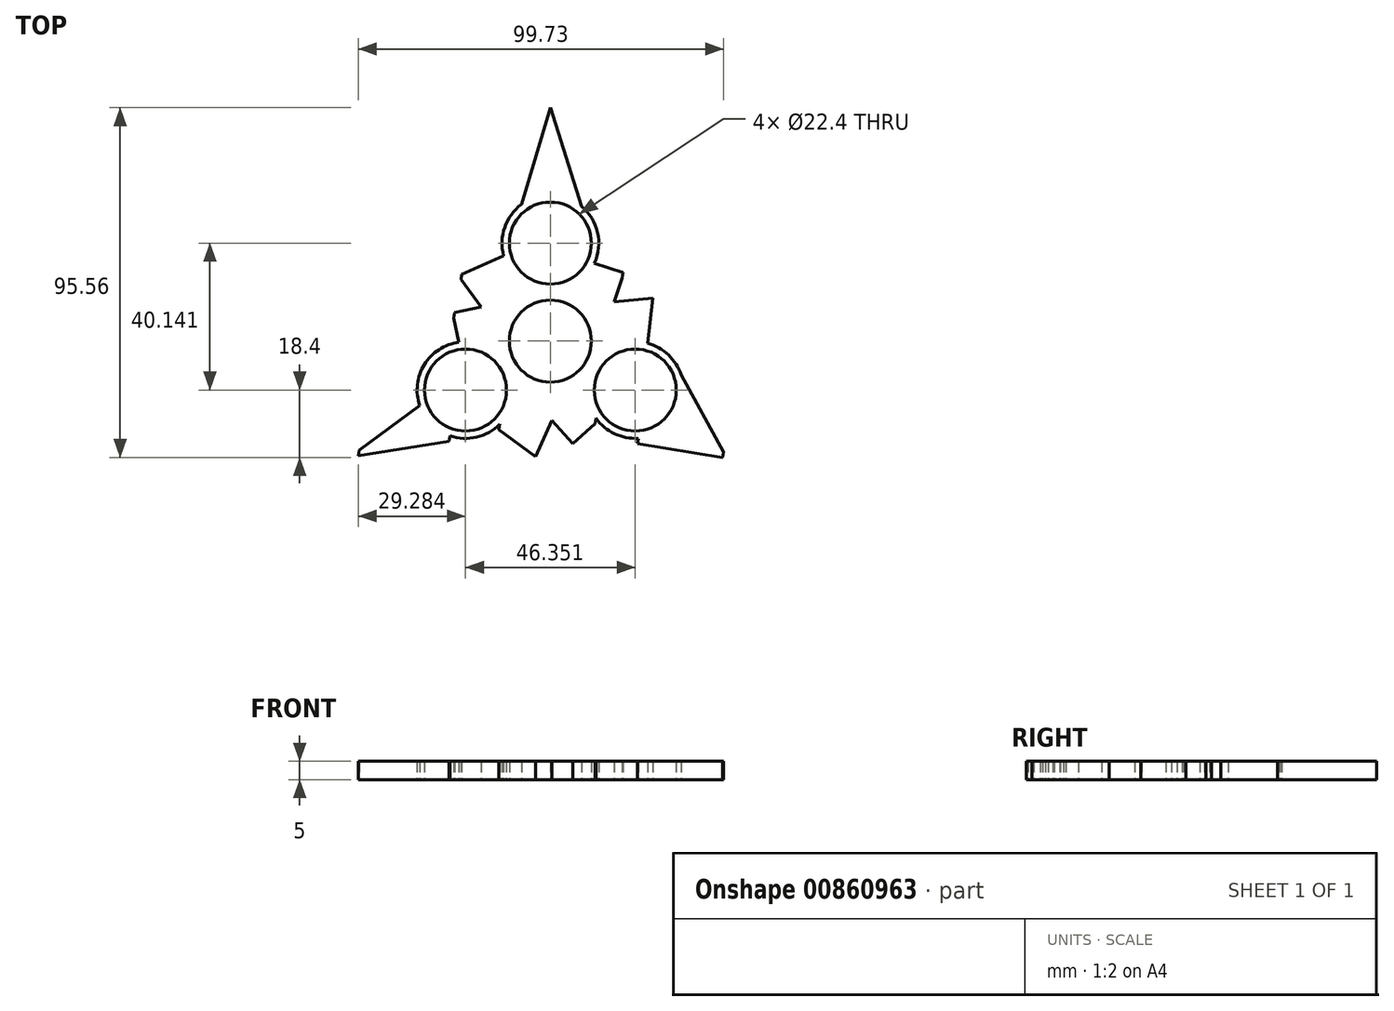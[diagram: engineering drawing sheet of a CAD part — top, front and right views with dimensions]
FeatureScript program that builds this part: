
annotation { "Feature Type Name" : "Feature", "Feature Type Description" : "" }
export const myFeature = defineFeature(function(context is Context, id is Id, definition is map)
    precondition{}
    {
        {
            var Q0;
            Q0=qCreatedBy(makeId("Top.planeOp"),FACE);
            var sketch = newSketch(context, id + "F0", { "sketchPlane" : qUnion([Q0])});
            skCircle(sketch, "E0", {"center": v(0, 0) * mm, "radius": 11.2 * mm});
            skCircle(sketch, "E1", {"center": v(0, 26.76) * mm, "radius": 11.2 * mm});
            skArc(sketch, "E2", {"start": v(12.02, 21.3) * mm, "mid": v(1.06, 39.92) * mm, "end": v(-12.74, 23.3) * mm});
            skArc(sketch, "E3.1.0", {"start": v(-24.46, -0.24) * mm, "mid": v(-35.1, -19.04) * mm, "end": v(-13.81, -22.68) * mm});
            skCircle(sketch, "E3.1.1", {"center": v(-23.18, -13.38) * mm, "radius": 11.2 * mm});
            skArc(sketch, "E3.2.0", {"start": v(12.44, -21.06) * mm, "mid": v(34.04, -20.88) * mm, "end": v(26.55, -0.62) * mm});
            skCircle(sketch, "E3.2.1", {"center": v(23.18, -13.38) * mm, "radius": 11.2 * mm});
            skLineSegment(sketch, "E4", {"start": v(-7.9, 37.34) * mm, "end": v(0, 63.78) * mm});
            skLineSegment(sketch, "E5", {"start": v(0, 63.78) * mm, "end": v(8.56, 36.8) * mm});
            skLineSegment(sketch, "E6", {"start": v(35.72, -9.27) * mm, "end": v(47.27, -30.3) * mm});
            skLineSegment(sketch, "E7", {"start": v(47.27, -30.3) * mm, "end": v(23.98, -26.56) * mm});
            skLineSegment(sketch, "E8", {"start": v(-35.69, -17.6) * mm, "end": v(-52.22, -29.83) * mm});
            skLineSegment(sketch, "E9", {"start": v(-52.22, -29.83) * mm, "end": v(-27.41, -25.88) * mm});
            skLineSegment(sketch, "E10", {"start": v(-12.74, 23.3) * mm, "end": v(-24.17, 18.27) * mm});
            skLineSegment(sketch, "E11", {"start": v(-24.17, 18.27) * mm, "end": v(-17.8, 9.55) * mm});
            skLineSegment(sketch, "E12", {"start": v(-17.8, 9.55) * mm, "end": v(-26.14, 7.8) * mm});
            skLineSegment(sketch, "E13", {"start": v(-26.14, 7.8) * mm, "end": v(-24.46, -0.24) * mm});
            skLineSegment(sketch, "E14.1.0", {"start": v(-13.81, -22.68) * mm, "end": v(-3.74, -30.07) * mm});
            skLineSegment(sketch, "E14.1.1", {"start": v(-3.74, -30.07) * mm, "end": v(0.63, -20.2) * mm});
            skLineSegment(sketch, "E14.1.2", {"start": v(0.63, -20.2) * mm, "end": v(6.31, -26.54) * mm});
            skLineSegment(sketch, "E14.1.3", {"start": v(6.31, -26.54) * mm, "end": v(12.44, -21.06) * mm});
            skLineSegment(sketch, "E14.2.0", {"start": v(26.55, -0.62) * mm, "end": v(27.9, 11.8) * mm});
            skLineSegment(sketch, "E14.2.1", {"start": v(27.9, 11.8) * mm, "end": v(17.17, 10.64) * mm});
            skLineSegment(sketch, "E14.2.2", {"start": v(17.17, 10.64) * mm, "end": v(19.83, 18.74) * mm});
            skLineSegment(sketch, "E14.2.3", {"start": v(19.83, 18.74) * mm, "end": v(12.02, 21.3) * mm});
            skSolve(sketch);
        }
        {
            var Q0;
            Q0=makeQuery(id+"F0.imprint","IMPRINT",FACE,{"disambiguationData":[TD([[makeQuery(id+"F0.imprint","IMPRINT",EDGE,{"derivedFrom":sQuery(id+"F0.wireOp",EDGE,"E0")}),-1.0]])]});
            var Q1;
            {var subQ0=sQuery(id+"F0.wireOp",EDGE,"E8");Q1=makeQuery(id+"F0.imprint","IMPRINT",FACE,{"disambiguationData":[TD([[makeQuery(id+"F0.imprint","IMPRINT",EDGE,{"derivedFrom":subQ0}),1.0]])]});}
            var Q2;
            {var subQ0=sQuery(id+"F0.wireOp",EDGE,"E6");Q2=makeQuery(id+"F0.imprint","IMPRINT",FACE,{"disambiguationData":[TD([[makeQuery(id+"F0.imprint","IMPRINT",EDGE,{"derivedFrom":subQ0}),-1.0]])]});}
            var Q3;
            {var subQ0=sQuery(id+"F0.wireOp",EDGE,"E4");Q3=makeQuery(id+"F0.imprint","IMPRINT",FACE,{"disambiguationData":[TD([[makeQuery(id+"F0.imprint","IMPRINT",EDGE,{"derivedFrom":subQ0}),-1.0]])]});}
            extrude(context, id + "F1", {"entities" : qUnion([Q0, Q1, Q2, Q3]), "depth" : 5 * mm, "offsetDistance" : 25 * mm});
        }
        {
            var Q0;
            Q0=makeQuery(id+"F1.opExtrude","SWEPT_FACE",FACE,{"disambiguationData":[OSD([sQuery(id+"F0.wireOp",EDGE,"E7")])]});
            var Q1;
            Q1=makeQuery(id+"F1.opExtrude","SWEPT_FACE",FACE,{"disambiguationData":[OSD([sQuery(id+"F0.wireOp",EDGE,"E6")])]});
            var Q2;
            Q2=makeQuery(id+"F1.opExtrude","SWEPT_FACE",FACE,{"disambiguationData":[OSD([sQuery(id+"F0.wireOp",EDGE,"E14.2.2")])]});
            var Q3;
            Q3=makeQuery(id+"F1.opExtrude","SWEPT_FACE",FACE,{"disambiguationData":[OSD([sQuery(id+"F0.wireOp",EDGE,"E5")])]});
            var Q4;
            Q4=makeQuery(id+"F1.opExtrude","SWEPT_FACE",FACE,{"disambiguationData":[OSD([sQuery(id+"F0.wireOp",EDGE,"E9")])]});
            var Q5;
            Q5=makeQuery(id+"F1.opExtrude","SWEPT_FACE",FACE,{"disambiguationData":[OSD([sQuery(id+"F0.wireOp",EDGE,"E14.1.1")])]});
            var Q6;
            Q6=makeQuery(id+"F1.opExtrude","SWEPT_FACE",FACE,{"disambiguationData":[OSD([sQuery(id+"F0.wireOp",EDGE,"E14.1.3")])]});
            var Q7;
            Q7=makeQuery(id+"F1.opExtrude","SWEPT_FACE",FACE,{"disambiguationData":[OSD([sQuery(id+"F0.wireOp",EDGE,"E14.1.0")])]});
            var Q8;
            Q8=makeQuery(id+"F1.opExtrude","SWEPT_FACE",FACE,{"disambiguationData":[OSD([sQuery(id+"F0.wireOp",EDGE,"E14.2.1")])]});
            var Q9;
            Q9=makeQuery(id+"F1.opExtrude","SWEPT_FACE",FACE,{"disambiguationData":[OSD([sQuery(id+"F0.wireOp",EDGE,"E14.2.0")])]});
            var Q10;
            Q10=makeQuery(id+"F1.opExtrude","SWEPT_FACE",FACE,{"disambiguationData":[OSD([sQuery(id+"F0.wireOp",EDGE,"E14.1.2")])]});
            var Q11;
            Q11=makeQuery(id+"F1.opExtrude","SWEPT_FACE",FACE,{"disambiguationData":[OSD([sQuery(id+"F0.wireOp",EDGE,"E13")])]});
            var Q12;
            Q12=makeQuery(id+"F1.opExtrude","SWEPT_FACE",FACE,{"disambiguationData":[OSD([sQuery(id+"F0.wireOp",EDGE,"E11")])]});
            var Q13;
            Q13=makeQuery(id+"F1.opExtrude","SWEPT_FACE",FACE,{"disambiguationData":[OSD([sQuery(id+"F0.wireOp",EDGE,"E4")])]});
            var Q14;
            Q14=makeQuery(id+"F1.opExtrude","SWEPT_FACE",FACE,{"disambiguationData":[OSD([sQuery(id+"F0.wireOp",EDGE,"E10")])]});
            var Q15;
            Q15=makeQuery(id+"F1.opExtrude","SWEPT_FACE",FACE,{"disambiguationData":[OSD([sQuery(id+"F0.wireOp",EDGE,"E12")])]});
            var Q16;
            Q16=makeQuery(id+"F1.opExtrude","SWEPT_FACE",FACE,{"disambiguationData":[OSD([sQuery(id+"F0.wireOp",EDGE,"E14.2.3")])]});
            extrude(context, id + "F2", {"entities" : qUnion([Q0, Q1, Q2, Q3, Q4, Q5, Q6, Q7, Q8, Q9, Q10, Q11, Q12, Q13, Q14, Q15, Q16]), "operationType" : NewBodyOperationType.ADD, "depth" : 1.5 * mm, "offsetDistance" : 25 * mm});
        }
    });
